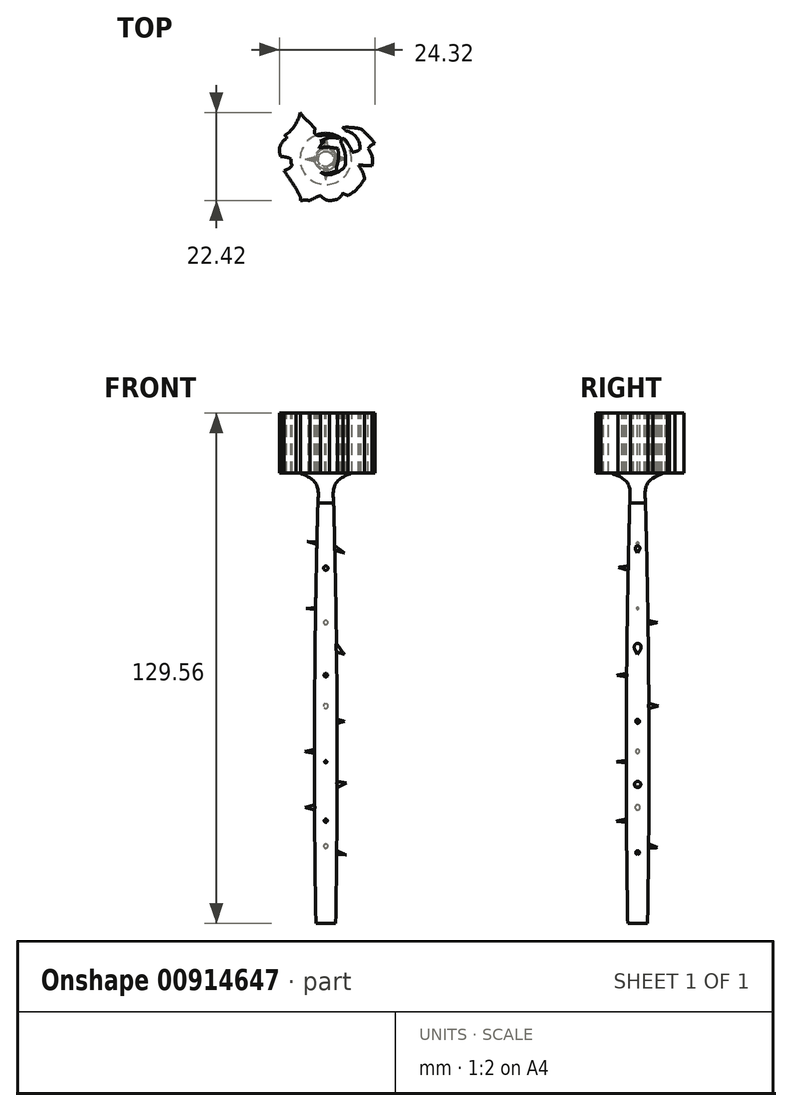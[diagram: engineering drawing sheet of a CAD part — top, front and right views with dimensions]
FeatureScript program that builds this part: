
annotation { "Feature Type Name" : "Feature", "Feature Type Description" : "" }
export const myFeature = defineFeature(function(context is Context, id is Id, definition is map)
    precondition{}
    {
        {
            var Q0;
            Q0=qCreatedBy(makeId("Front.planeOp"),FACE);
            var sketch = newSketch(context, id + "F0", { "sketchPlane" : qUnion([Q0])});
            skLineSegment(sketch, "E0", {"start": v(0, 50.56) * mm, "end": v(0, -56.14) * mm});
            skLineSegment(sketch, "E1", {"start": v(0, 50.56) * mm, "end": v(-2, 50.56) * mm});
            skLineSegment(sketch, "E2", {"start": v(0, -56.14) * mm, "end": v(-2.52, -56.14) * mm});
            skArc(sketch, "E3", {"start": v(-2, 50.56) * mm, "mid": v(-2.86, -2.8) * mm, "end": v(-2.52, -56.14) * mm});
            skLineSegment(sketch, "E4", {"start": v(0, 50.56) * mm, "end": v(0, -56.14) * mm, "construction": true});
            skSolve(sketch);
        }
        {
            var Q0;
            Q0=makeQuery(id+"F0.imprint","IMPRINT",FACE,{"disambiguationData":[TD([[makeQuery(id+"F0.imprint","IMPRINT",EDGE,{"derivedFrom":sQuery(id+"F0.wireOp",EDGE,"E0")}),-1.0]])]});
            var Q1;
            Q1=sQuery(id+"F0.wireOp",EDGE,"E0");
            revolve(context, id + "F1", {"surfaceOperationType" : NewSurfaceOperationType.NEW, "entities" : qUnion([Q0]), "axis" : qUnion([Q1]), "revolveType" : RevolveType.FULL});
        }
        {
            var Q0;
            Q0=qCreatedBy(makeId("Front.planeOp"),FACE);
            var sketch = newSketch(context, id + "F2", { "sketchPlane" : qUnion([Q0])});
            skLineSegment(sketch, "E5", {"start": v(-2.2, 40.38) * mm, "end": v(-2.19, 40.64) * mm});
            skLineSegment(sketch, "E6", {"start": v(-2.2, 40.38) * mm, "end": v(-4.73, 40.83) * mm});
            skLineSegment(sketch, "E7", {"start": v(2.21, 39.1) * mm, "end": v(4.78, 37.88) * mm});
            skLineSegment(sketch, "E8", {"start": v(4.78, 37.88) * mm, "end": v(2.24, 39.78) * mm});
            skLineSegment(sketch, "E9", {"start": v(-2.48, 24.12) * mm, "end": v(-5.02, 23.87) * mm});
            skLineSegment(sketch, "E10", {"start": v(-5.02, 23.87) * mm, "end": v(-2.48, 23.84) * mm});
            skLineSegment(sketch, "E11", {"start": v(-2.48, 23.84) * mm, "end": v(-2.48, 24.12) * mm});
            skLineSegment(sketch, "E12", {"start": v(2.24, 39.78) * mm, "end": v(2.21, 39.1) * mm});
            skLineSegment(sketch, "E13", {"start": v(-2.19, 40.64) * mm, "end": v(-4.73, 40.83) * mm});
            skLineSegment(sketch, "E14", {"start": v(2.24, 15.55) * mm, "end": v(2.24, 13.97) * mm});
            skLineSegment(sketch, "E15", {"start": v(2.24, 13.97) * mm, "end": v(4.78, 12.08) * mm});
            skLineSegment(sketch, "E16", {"start": v(4.78, 12.08) * mm, "end": v(2.24, 15.55) * mm});
            skLineSegment(sketch, "E17", {"start": v(2.24, -4.22) * mm, "end": v(4.78, -4.87) * mm});
            skLineSegment(sketch, "E18", {"start": v(4.78, -4.87) * mm, "end": v(2.75, -4.87) * mm});
            skLineSegment(sketch, "E19", {"start": v(-2.78, -11.98) * mm, "end": v(-5.32, -12.55) * mm});
            skLineSegment(sketch, "E20", {"start": v(-5.32, -12.55) * mm, "end": v(-2.8, -12.49) * mm});
            skLineSegment(sketch, "E21", {"start": v(-2.8, -12.49) * mm, "end": v(-2.78, -11.98) * mm});
            skLineSegment(sketch, "E22", {"start": v(2.7, -20.1) * mm, "end": v(5.25, -20.55) * mm});
            skLineSegment(sketch, "E23", {"start": v(5.25, -20.55) * mm, "end": v(2.8, -20.9) * mm});
            skLineSegment(sketch, "E24", {"start": v(2.8, -20.9) * mm, "end": v(2.7, -20.1) * mm});
            skLineSegment(sketch, "E25", {"start": v(-2.78, -26.09) * mm, "end": v(-5.32, -26.73) * mm});
            skLineSegment(sketch, "E26", {"start": v(-5.32, -26.73) * mm, "end": v(-2.78, -26.73) * mm});
            skLineSegment(sketch, "E27", {"start": v(-2.78, -26.73) * mm, "end": v(-2.78, -26.09) * mm});
            skLineSegment(sketch, "E28", {"start": v(2.7, -37.7) * mm, "end": v(5.25, -38.83) * mm});
            skLineSegment(sketch, "E29", {"start": v(5.25, -38.83) * mm, "end": v(2.7, -38.22) * mm});
            skLineSegment(sketch, "E30", {"start": v(2.7, -38.22) * mm, "end": v(2.7, -37.7) * mm});
            skLineSegment(sketch, "E31", {"start": v(-5.32, -26.73) * mm, "end": v(-2.78, -26.73) * mm, "construction": true});
            skLineSegment(sketch, "E32", {"start": v(5.25, -20.55) * mm, "end": v(2.8, -20.9) * mm, "construction": true});
            skLineSegment(sketch, "E33", {"start": v(5.25, -38.83) * mm, "end": v(2.7, -38.22) * mm, "construction": true});
            skLineSegment(sketch, "E34", {"start": v(-5.32, -12.55) * mm, "end": v(-2.8, -12.49) * mm, "construction": true});
            skLineSegment(sketch, "E35", {"start": v(4.78, -4.87) * mm, "end": v(2.75, -4.87) * mm, "construction": true});
            skLineSegment(sketch, "E36", {"start": v(2.24, 13.97) * mm, "end": v(4.78, 12.08) * mm, "construction": true});
            skLineSegment(sketch, "E37", {"start": v(-5.02, 23.87) * mm, "end": v(-2.48, 23.84) * mm, "construction": true});
            skLineSegment(sketch, "E38", {"start": v(4.78, 37.88) * mm, "end": v(2.24, 39.78) * mm, "construction": true});
            skLineSegment(sketch, "E39", {"start": v(-2.2, 40.38) * mm, "end": v(-4.73, 40.83) * mm, "construction": true});
            skLineSegment(sketch, "E40", {"start": v(2.75, -4.87) * mm, "end": v(2.24, -4.22) * mm});
            skSolve(sketch);
        }
        {
            var Q0;
            Q0=makeQuery(id+"F2.imprint","IMPRINT",FACE,{"disambiguationData":[TD([[makeQuery(id+"F2.imprint","IMPRINT",EDGE,{"derivedFrom":sQuery(id+"F2.wireOp",EDGE,"E28")}),-1.0]])]});
            var Q1;
            Q1=sQuery(id+"F2.wireOp",EDGE,"E29");
            revolve(context, id + "F3", {"operationType" : NewBodyOperationType.ADD, "surfaceOperationType" : NewSurfaceOperationType.NEW, "entities" : qUnion([Q0]), "axis" : qUnion([Q1]), "revolveType" : RevolveType.FULL});
        }
        {
            var Q0;
            Q0=makeQuery(id+"F2.imprint","IMPRINT",FACE,{"disambiguationData":[TD([[makeQuery(id+"F2.imprint","IMPRINT",EDGE,{"derivedFrom":sQuery(id+"F2.wireOp",EDGE,"E25")}),1.0]])]});
            var Q1;
            Q1=sQuery(id+"F2.wireOp",EDGE,"E26");
            revolve(context, id + "F4", {"operationType" : NewBodyOperationType.ADD, "surfaceOperationType" : NewSurfaceOperationType.NEW, "entities" : qUnion([Q0]), "axis" : qUnion([Q1]), "revolveType" : RevolveType.FULL});
        }
        {
            var Q0;
            Q0=makeQuery(id+"F2.imprint","IMPRINT",FACE,{"disambiguationData":[TD([[makeQuery(id+"F2.imprint","IMPRINT",EDGE,{"derivedFrom":sQuery(id+"F2.wireOp",EDGE,"E22")}),-1.0]])]});
            var Q1;
            Q1=sQuery(id+"F2.wireOp",EDGE,"E23");
            revolve(context, id + "F5", {"operationType" : NewBodyOperationType.ADD, "surfaceOperationType" : NewSurfaceOperationType.NEW, "entities" : qUnion([Q0]), "axis" : qUnion([Q1]), "revolveType" : RevolveType.FULL});
        }
        {
            var Q0;
            Q0=makeQuery(id+"F2.imprint","IMPRINT",FACE,{"disambiguationData":[TD([[makeQuery(id+"F2.imprint","IMPRINT",EDGE,{"derivedFrom":sQuery(id+"F2.wireOp",EDGE,"E19")}),1.0]])]});
            var Q1;
            Q1=sQuery(id+"F2.wireOp",EDGE,"E20");
            revolve(context, id + "F6", {"operationType" : NewBodyOperationType.ADD, "surfaceOperationType" : NewSurfaceOperationType.NEW, "entities" : qUnion([Q0]), "axis" : qUnion([Q1]), "revolveType" : RevolveType.FULL});
        }
        {
            var Q0;
            Q0=makeQuery(id+"F2.imprint","IMPRINT",FACE,{"disambiguationData":[TD([[makeQuery(id+"F2.imprint","IMPRINT",EDGE,{"derivedFrom":sQuery(id+"F2.wireOp",EDGE,"E17")}),-1.0]])]});
            var Q1;
            Q1=sQuery(id+"F2.wireOp",EDGE,"E18");
            revolve(context, id + "F7", {"operationType" : NewBodyOperationType.ADD, "surfaceOperationType" : NewSurfaceOperationType.NEW, "entities" : qUnion([Q0]), "axis" : qUnion([Q1]), "revolveType" : RevolveType.FULL});
        }
        {
            var Q0;
            Q0=makeQuery(id+"F2.imprint","IMPRINT",FACE,{"disambiguationData":[TD([[makeQuery(id+"F2.imprint","IMPRINT",EDGE,{"derivedFrom":sQuery(id+"F2.wireOp",EDGE,"E14")}),1.0]])]});
            var Q1;
            Q1=sQuery(id+"F2.wireOp",EDGE,"E15");
            revolve(context, id + "F8", {"operationType" : NewBodyOperationType.ADD, "surfaceOperationType" : NewSurfaceOperationType.NEW, "entities" : qUnion([Q0]), "axis" : qUnion([Q1]), "revolveType" : RevolveType.FULL});
        }
        {
            var Q0;
            Q0=makeQuery(id+"F2.imprint","IMPRINT",FACE,{"disambiguationData":[TD([[makeQuery(id+"F2.imprint","IMPRINT",EDGE,{"derivedFrom":sQuery(id+"F2.wireOp",EDGE,"E9")}),1.0]])]});
            var Q1;
            Q1=sQuery(id+"F2.wireOp",EDGE,"E10");
            revolve(context, id + "F9", {"operationType" : NewBodyOperationType.ADD, "surfaceOperationType" : NewSurfaceOperationType.NEW, "entities" : qUnion([Q0]), "axis" : qUnion([Q1]), "revolveType" : RevolveType.FULL});
        }
        {
            var Q0;
            Q0=makeQuery(id+"F2.imprint","IMPRINT",FACE,{"disambiguationData":[TD([[makeQuery(id+"F2.imprint","IMPRINT",EDGE,{"derivedFrom":sQuery(id+"F2.wireOp",EDGE,"E7")}),1.0]])]});
            var Q1;
            Q1=sQuery(id+"F2.wireOp",EDGE,"E7");
            revolve(context, id + "F10", {"operationType" : NewBodyOperationType.ADD, "surfaceOperationType" : NewSurfaceOperationType.NEW, "entities" : qUnion([Q0]), "axis" : qUnion([Q1]), "revolveType" : RevolveType.FULL});
        }
        {
            var Q0;
            Q0=makeQuery(id+"F2.imprint","IMPRINT",FACE,{"disambiguationData":[TD([[makeQuery(id+"F2.imprint","IMPRINT",EDGE,{"derivedFrom":sQuery(id+"F2.wireOp",EDGE,"E5")}),1.0]])]});
            var Q1;
            Q1=sQuery(id+"F2.wireOp",EDGE,"E6");
            revolve(context, id + "F11", {"operationType" : NewBodyOperationType.ADD, "surfaceOperationType" : NewSurfaceOperationType.NEW, "entities" : qUnion([Q0]), "axis" : qUnion([Q1]), "revolveType" : RevolveType.FULL});
        }
        {
            var Q0;
            Q0=qCreatedBy(makeId("Right.planeOp"),FACE);
            var sketch = newSketch(context, id + "F12", { "sketchPlane" : qUnion([Q0])});
            skLineSegment(sketch, "E41", {"start": v(-2.3, 34.62) * mm, "end": v(-4.83, 34.27) * mm});
            skLineSegment(sketch, "E42", {"start": v(-4.83, 34.27) * mm, "end": v(-2.3, 34.06) * mm});
            skLineSegment(sketch, "E43", {"start": v(-2.3, 34.06) * mm, "end": v(-2.3, 34.62) * mm});
            skLineSegment(sketch, "E44", {"start": v(2.44, 20.8) * mm, "end": v(4.98, 20.23) * mm});
            skLineSegment(sketch, "E45", {"start": v(4.98, 20.23) * mm, "end": v(2.51, 20.23) * mm});
            skLineSegment(sketch, "E46", {"start": v(2.51, 20.23) * mm, "end": v(2.44, 20.8) * mm});
            skLineSegment(sketch, "E47", {"start": v(-2.7, 7.32) * mm, "end": v(-5.25, 6.85) * mm});
            skLineSegment(sketch, "E48", {"start": v(-5.25, 6.85) * mm, "end": v(-2.7, 6.85) * mm});
            skLineSegment(sketch, "E49", {"start": v(-2.7, 6.85) * mm, "end": v(-2.7, 7.32) * mm});
            skLineSegment(sketch, "E50", {"start": v(-2.82, -14.85) * mm, "end": v(-5.36, -15.13) * mm});
            skLineSegment(sketch, "E51", {"start": v(-5.36, -15.13) * mm, "end": v(-2.83, -15.13) * mm});
            skLineSegment(sketch, "E52", {"start": v(-2.83, -15.13) * mm, "end": v(-2.82, -14.85) * mm});
            skLineSegment(sketch, "E53", {"start": v(-2.86, -29.71) * mm, "end": v(-5.4, -30.23) * mm});
            skLineSegment(sketch, "E54", {"start": v(-5.4, -30.23) * mm, "end": v(-2.8, -30.1) * mm});
            skLineSegment(sketch, "E55", {"start": v(-2.8, -30.1) * mm, "end": v(-2.86, -29.71) * mm});
            skLineSegment(sketch, "E56", {"start": v(2.65, -0.32) * mm, "end": v(5.25, -0.97) * mm});
            skLineSegment(sketch, "E57", {"start": v(5.25, -0.97) * mm, "end": v(2.71, -0.97) * mm});
            skLineSegment(sketch, "E58", {"start": v(2.71, -0.97) * mm, "end": v(2.65, -0.32) * mm});
            skLineSegment(sketch, "E59", {"start": v(2.54, -35.96) * mm, "end": v(5.08, -36.94) * mm});
            skLineSegment(sketch, "E60", {"start": v(5.08, -36.94) * mm, "end": v(2.6, -36.57) * mm});
            skLineSegment(sketch, "E61", {"start": v(2.6, -36.57) * mm, "end": v(2.54, -35.96) * mm});
            skSolve(sketch);
        }
        {
            var Q0;
            Q0=makeQuery(id+"F12.imprint","IMPRINT",FACE,{"disambiguationData":[TD([[makeQuery(id+"F12.imprint","IMPRINT",EDGE,{"derivedFrom":sQuery(id+"F12.wireOp",EDGE,"E59")}),-1.0]])]});
            var Q1;
            Q1=sQuery(id+"F12.wireOp",EDGE,"E60");
            revolve(context, id + "F13", {"operationType" : NewBodyOperationType.ADD, "surfaceOperationType" : NewSurfaceOperationType.NEW, "entities" : qUnion([Q0]), "axis" : qUnion([Q1]), "revolveType" : RevolveType.FULL});
        }
        {
            var Q0;
            Q0=makeQuery(id+"F12.imprint","IMPRINT",FACE,{"disambiguationData":[TD([[makeQuery(id+"F12.imprint","IMPRINT",EDGE,{"derivedFrom":sQuery(id+"F12.wireOp",EDGE,"E53")}),1.0]])]});
            var Q1;
            Q1=sQuery(id+"F12.wireOp",EDGE,"E54");
            revolve(context, id + "F14", {"operationType" : NewBodyOperationType.ADD, "surfaceOperationType" : NewSurfaceOperationType.NEW, "entities" : qUnion([Q0]), "axis" : qUnion([Q1]), "revolveType" : RevolveType.FULL});
        }
        {
            var Q0;
            Q0=makeQuery(id+"F12.imprint","IMPRINT",FACE,{"disambiguationData":[TD([[makeQuery(id+"F12.imprint","IMPRINT",EDGE,{"derivedFrom":sQuery(id+"F12.wireOp",EDGE,"E50")}),1.0]])]});
            var Q1;
            Q1=sQuery(id+"F12.wireOp",EDGE,"E51");
            revolve(context, id + "F15", {"operationType" : NewBodyOperationType.ADD, "surfaceOperationType" : NewSurfaceOperationType.NEW, "entities" : qUnion([Q0]), "axis" : qUnion([Q1]), "revolveType" : RevolveType.FULL});
        }
        {
            var Q0;
            Q0=makeQuery(id+"F12.imprint","IMPRINT",FACE,{"disambiguationData":[TD([[makeQuery(id+"F12.imprint","IMPRINT",EDGE,{"derivedFrom":sQuery(id+"F12.wireOp",EDGE,"E56")}),-1.0]])]});
            var Q1;
            Q1=sQuery(id+"F12.wireOp",EDGE,"E57");
            revolve(context, id + "F16", {"operationType" : NewBodyOperationType.ADD, "surfaceOperationType" : NewSurfaceOperationType.NEW, "entities" : qUnion([Q0]), "axis" : qUnion([Q1]), "revolveType" : RevolveType.FULL});
        }
        {
            var Q0;
            Q0=makeQuery(id+"F12.imprint","IMPRINT",FACE,{"disambiguationData":[TD([[makeQuery(id+"F12.imprint","IMPRINT",EDGE,{"derivedFrom":sQuery(id+"F12.wireOp",EDGE,"E47")}),1.0]])]});
            var Q1;
            Q1=sQuery(id+"F12.wireOp",EDGE,"E48");
            revolve(context, id + "F17", {"operationType" : NewBodyOperationType.ADD, "surfaceOperationType" : NewSurfaceOperationType.NEW, "entities" : qUnion([Q0]), "axis" : qUnion([Q1]), "revolveType" : RevolveType.FULL});
        }
        {
            var Q0;
            Q0=makeQuery(id+"F12.imprint","IMPRINT",FACE,{"disambiguationData":[TD([[makeQuery(id+"F12.imprint","IMPRINT",EDGE,{"derivedFrom":sQuery(id+"F12.wireOp",EDGE,"E44")}),-1.0]])]});
            var Q1;
            Q1=sQuery(id+"F12.wireOp",EDGE,"E45");
            revolve(context, id + "F18", {"operationType" : NewBodyOperationType.ADD, "surfaceOperationType" : NewSurfaceOperationType.NEW, "entities" : qUnion([Q0]), "axis" : qUnion([Q1]), "revolveType" : RevolveType.FULL});
        }
        {
            var Q0;
            Q0=makeQuery(id+"F12.imprint","IMPRINT",FACE,{"disambiguationData":[TD([[makeQuery(id+"F12.imprint","IMPRINT",EDGE,{"derivedFrom":sQuery(id+"F12.wireOp",EDGE,"E41")}),1.0]])]});
            var Q1;
            Q1=sQuery(id+"F12.wireOp",EDGE,"E42");
            revolve(context, id + "F19", {"operationType" : NewBodyOperationType.ADD, "surfaceOperationType" : NewSurfaceOperationType.NEW, "entities" : qUnion([Q0]), "axis" : qUnion([Q1]), "revolveType" : RevolveType.FULL});
        }
        {
            var Q0;
            Q0=makeQuery(id+"F1.opRevolve","SWEPT_FACE",FACE,{"disambiguationData":[OSD([sQuery(id+"F0.wireOp",EDGE,"E1")])]});
            cPlane(context, id + "F20", {"entities" : qUnion([Q0]), "cplaneType" : CPlaneType.OFFSET, "offset" : 76.2 * mm, "width" : 152.4 * mm, "height" : 152.4 * mm});
        }
        {
            var Q0;
            Q0=makeQuery(id+"F1.opRevolve","SWEPT_FACE",FACE,{"disambiguationData":[OSD([sQuery(id+"F0.wireOp",EDGE,"E1")])]});
            cPlane(context, id + "F21", {"entities" : qUnion([Q0]), "cplaneType" : CPlaneType.OFFSET, "offset" : 22.86 * mm, "width" : 152.4 * mm, "height" : 152.4 * mm});
        }
        {
            var Q0;
            Q0=qCreatedBy(id+"F21.planeOp",FACE);
            var sketch = newSketch(context, id + "F22", { "sketchPlane" : qUnion([Q0])});
            skCircle(sketch, "E62", {"center": v(0, 0) * mm, "radius": 10.65 * mm});
            skLineSegment(sketch, "E63", {"start": v(0, 10.65) * mm, "end": v(0, -10.65) * mm, "construction": true});
            skSolve(sketch);
        }
        {
            var Q0;
            Q0=makeQuery(id+"F22.imprint","IMPRINT",FACE,{"disambiguationData":[TD([[makeQuery(id+"F22.imprint","IMPRINT",EDGE,{"derivedFrom":sQuery(id+"F22.wireOp",EDGE,"E62")}),1.0]])]});
            cPlane(context, id + "F23", {"entities" : qUnion([Q0]), "cplaneType" : CPlaneType.OFFSET, "offset" : 15.24 * mm, "oppositeDirection" : true, "width" : 152.4 * mm, "height" : 152.4 * mm});
        }
        {
            var Q0;
            Q0=qCreatedBy(id+"F23.planeOp",FACE);
            var sketch = newSketch(context, id + "F24", { "sketchPlane" : qUnion([Q0])});
            skCircle(sketch, "E64", {"center": v(0, 0) * mm, "radius": 6.51 * mm});
            skSolve(sketch);
        }
        {
            var Q0;
            Q0=makeQuery(id+"F22.imprint","IMPRINT",FACE,{"disambiguationData":[TD([[makeQuery(id+"F22.imprint","IMPRINT",EDGE,{"derivedFrom":sQuery(id+"F22.wireOp",EDGE,"E62")}),1.0]])]});
            cPlane(context, id + "F25", {"entities" : qUnion([Q0]), "cplaneType" : CPlaneType.OFFSET, "offset" : 17.78 * mm, "oppositeDirection" : true, "width" : 152.4 * mm, "height" : 152.4 * mm});
        }
        {
            var Q0;
            Q0=qCreatedBy(id+"F25.planeOp",FACE);
            var sketch = newSketch(context, id + "F26", { "sketchPlane" : qUnion([Q0])});
            skCircle(sketch, "E65", {"center": v(0, 0) * mm, "radius": 2.54 * mm});
            skSolve(sketch);
        }
        {
            var Q1;
            Q1=makeQuery(id+"F1.opRevolve","SWEPT_FACE",FACE,{"disambiguationData":[OSD([sQuery(id+"F0.wireOp",EDGE,"E1")])]});
            var Q2;
            Q2=makeQuery(id+"F26.imprint","IMPRINT",FACE,{"disambiguationData":[TD([[makeQuery(id+"F26.imprint","IMPRINT",EDGE,{"derivedFrom":sQuery(id+"F26.wireOp",EDGE,"E65")}),1.0]])]});
            var Q3;
            Q3=makeQuery(id+"F24.imprint","IMPRINT",FACE,{"disambiguationData":[TD([[makeQuery(id+"F24.imprint","IMPRINT",EDGE,{"derivedFrom":sQuery(id+"F24.wireOp",EDGE,"E64")}),1.0]])]});
            loft(context, id + "F27", {"operationType" : NewBodyOperationType.ADD, "sheetProfilesArray" : [{ "sheetProfileEntities" : qUnion([Q1]) }, { "sheetProfileEntities" : qUnion([Q2]) }, { "sheetProfileEntities" : qUnion([Q3]) }]});
        }
        {
            var Q0;
            Q0=sQuery(id+"F22.wireOp",EDGE,"E63");
            cPlane(context, id + "F28", {"entities" : qUnion([Q0]), "cplaneType" : CPlaneType.LINE_ANGLE, "offset" : 25.4 * mm, "angle" : 90 * degree, "width" : 152.4 * mm, "height" : 152.4 * mm});
        }
        {
            var Q0;
            Q0=makeQuery(id+"F22.imprint","IMPRINT",FACE,{"disambiguationData":[TD([[makeQuery(id+"F22.imprint","IMPRINT",EDGE,{"derivedFrom":sQuery(id+"F22.wireOp",EDGE,"E62")}),1.0]])]});
            var sketch = newSketch(context, id + "F29", { "sketchPlane" : qUnion([Q0])});
            skArc(sketch, "E66", {"start": v(-10.3, 6.03) * mm, "mid": v(-7.83, 8.55) * mm, "end": v(-6.5, 11.82) * mm});
            skArc(sketch, "E67", {"start": v(-10.3, 6.03) * mm, "mid": v(-10.2, 5.76) * mm, "end": v(-9.93, 5.67) * mm});
            skArc(sketch, "E68", {"start": v(-10.05, 5.2) * mm, "mid": v(-9.93, 5.42) * mm, "end": v(-9.93, 5.67) * mm});
            skArc(sketch, "E69", {"start": v(-10.05, 5.2) * mm, "mid": v(-11.26, 3.94) * mm, "end": v(-11.8, 2.28) * mm});
            skArc(sketch, "E70", {"start": v(-11.8, 2.28) * mm, "mid": v(-11.68, 1.4) * mm, "end": v(-11.44, 0.54) * mm});
            skArc(sketch, "E71", {"start": v(-8.89, 0) * mm, "mid": v(-10.12, 0.48) * mm, "end": v(-11.44, 0.54) * mm});
            skLineSegment(sketch, "E72", {"start": v(-8.89, 0) * mm, "end": v(-8.89, -1.06) * mm});
            skArc(sketch, "E73", {"start": v(-8.56, -1.63) * mm, "mid": v(-8.7, -1.33) * mm, "end": v(-8.89, -1.06) * mm});
            skArc(sketch, "E74", {"start": v(-10.65, -2.93) * mm, "mid": v(-9.48, -2.49) * mm, "end": v(-8.56, -1.63) * mm});
            skArc(sketch, "E75", {"start": v(-7.62, -7.46) * mm, "mid": v(-9.12, -5.18) * mm, "end": v(-10.65, -2.93) * mm});
            skArc(sketch, "E76", {"start": v(-6.36, -9.89) * mm, "mid": v(-6.95, -8.66) * mm, "end": v(-7.62, -7.46) * mm});
            skLineSegment(sketch, "E77", {"start": v(-6.36, -9.89) * mm, "end": v(-6.36, -10.57) * mm});
            skArc(sketch, "E78", {"start": v(-4, -10.57) * mm, "mid": v(-5.17, -10.48) * mm, "end": v(-6.36, -10.57) * mm});
            skArc(sketch, "E79", {"start": v(-1.28, -9.28) * mm, "mid": v(-2.67, -9.85) * mm, "end": v(-4, -10.57) * mm});
            skArc(sketch, "E80", {"start": v(-1.28, -9.28) * mm, "mid": v(1.7, -10.61) * mm, "end": v(4.36, -8.71) * mm});
            skArc(sketch, "E81", {"start": v(4.36, -8.71) * mm, "mid": v(4.99, -9.03) * mm, "end": v(5.65, -9.28) * mm});
            skArc(sketch, "E82", {"start": v(5.65, -9.28) * mm, "mid": v(8.09, -7.47) * mm, "end": v(9.83, -4.97) * mm});
            skArc(sketch, "E83", {"start": v(9.83, -4.97) * mm, "mid": v(8.82, -2.33) * mm, "end": v(6.88, -0.27) * mm});
            skArc(sketch, "E84", {"start": v(11.73, -1.76) * mm, "mid": v(11.8, 0.54) * mm, "end": v(10.78, 2.6) * mm});
            skArc(sketch, "E85", {"start": v(12.51, 3.95) * mm, "mid": v(11.51, 3.45) * mm, "end": v(10.78, 2.6) * mm});
            skArc(sketch, "E86", {"start": v(12.51, 3.95) * mm, "mid": v(10.8, 5.87) * mm, "end": v(8.9, 7.6) * mm});
            skArc(sketch, "E87", {"start": v(5.56, -2.84) * mm, "mid": v(6.42, -1.66) * mm, "end": v(6.88, -0.27) * mm});
            skArc(sketch, "E88", {"start": v(3.92, -6.76) * mm, "mid": v(5.27, -5.02) * mm, "end": v(5.56, -2.84) * mm});
            skArc(sketch, "E89", {"start": v(2.15, -7.14) * mm, "mid": v(3.07, -7.08) * mm, "end": v(3.92, -6.76) * mm});
            skArc(sketch, "E90", {"start": v(1.36, -5.2) * mm, "mid": v(1.56, -6.25) * mm, "end": v(2.15, -7.14) * mm});
            skArc(sketch, "E91", {"start": v(1.36, -5.2) * mm, "mid": v(3.35, -3.67) * mm, "end": v(4.93, -1.71) * mm});
            skArc(sketch, "E92", {"start": v(-8.56, -1.63) * mm, "mid": v(-7.28, -5.09) * mm, "end": v(-4.83, -7.84) * mm});
            skArc(sketch, "E93", {"start": v(-7.2, 4.12) * mm, "mid": v(-8.45, 2.22) * mm, "end": v(-8.89, 0) * mm});
            skArc(sketch, "E94", {"start": v(-4.73, 3.74) * mm, "mid": v(-5.9, 4.4) * mm, "end": v(-7.2, 4.12) * mm});
            skArc(sketch, "E95", {"start": v(-4.73, 3.74) * mm, "mid": v(-6, 2.09) * mm, "end": v(-6.08, 0) * mm});
            skArc(sketch, "E96", {"start": v(-4.83, -7.84) * mm, "mid": v(-3.56, -8.21) * mm, "end": v(-2.4, -7.56) * mm});
            skArc(sketch, "E97", {"start": v(-2.4, -7.56) * mm, "mid": v(-1.92, -8.48) * mm, "end": v(-1.28, -9.28) * mm});
            skArc(sketch, "E98", {"start": v(6.88, -0.27) * mm, "mid": v(6.72, 1.76) * mm, "end": v(5.8, 3.57) * mm});
            skArc(sketch, "E99", {"start": v(5.8, 3.57) * mm, "mid": v(5.3, 4.44) * mm, "end": v(4.63, 5.18) * mm});
            skArc(sketch, "E100", {"start": v(1.25, 6.13) * mm, "mid": v(-2.02, 5.64) * mm, "end": v(-4.73, 3.74) * mm});
            skArc(sketch, "E101", {"start": v(3.36, 5.68) * mm, "mid": v(2.32, 5.95) * mm, "end": v(1.25, 6.13) * mm});
            skArc(sketch, "E102", {"start": v(-2.4, -7.56) * mm, "mid": v(-1.73, -5.47) * mm, "end": v(-1.99, -3.3) * mm});
            skArc(sketch, "E103", {"start": v(-4.6, -2.9) * mm, "mid": v(-3.3, -3.16) * mm, "end": v(-1.99, -3.3) * mm});
            skArc(sketch, "E104", {"start": v(-6.2, -1.06) * mm, "mid": v(-5.5, -2.09) * mm, "end": v(-4.57, -2.9) * mm});
            skArc(sketch, "E105", {"start": v(-5.73, -0.44) * mm, "mid": v(-6.11, -0.64) * mm, "end": v(-6.2, -1.06) * mm});
            skArc(sketch, "E106", {"start": v(-4.81, -0.44) * mm, "mid": v(-5.27, -0.37) * mm, "end": v(-5.73, -0.44) * mm});
            skArc(sketch, "E107", {"start": v(0, -4.03) * mm, "mid": v(2.76, -3.5) * mm, "end": v(4.93, -1.71) * mm});
            skArc(sketch, "E108", {"start": v(-1.28, -3.35) * mm, "mid": v(-0.68, -3.77) * mm, "end": v(0, -4.03) * mm});
            skLineSegment(sketch, "E109", {"start": v(-1.28, -3.35) * mm, "end": v(-1.99, -3.3) * mm});
            skArc(sketch, "E110", {"start": v(4.93, -1.71) * mm, "mid": v(4.7, -1.45) * mm, "end": v(4.37, -1.51) * mm});
            skArc(sketch, "E111", {"start": v(1, -3.54) * mm, "mid": v(2.87, -2.83) * mm, "end": v(4.37, -1.51) * mm});
            skArc(sketch, "E112", {"start": v(-2.3, -0.52) * mm, "mid": v(-0.84, -2.24) * mm, "end": v(1, -3.54) * mm});
            skArc(sketch, "E113", {"start": v(-2.48, 0.28) * mm, "mid": v(-2.5, -0.15) * mm, "end": v(-2.3, -0.52) * mm});
            skArc(sketch, "E114", {"start": v(-0.24, 4.56) * mm, "mid": v(-1.82, 2.66) * mm, "end": v(-2.48, 0.28) * mm});
            skArc(sketch, "E115", {"start": v(-6.08, 0) * mm, "mid": v(-5.6, -0.11) * mm, "end": v(-5.14, 0.05) * mm});
            skArc(sketch, "E116", {"start": v(-1.98, 4.15) * mm, "mid": v(-3.9, 2.37) * mm, "end": v(-5.14, 0.05) * mm});
            skLineSegment(sketch, "E117", {"start": v(-1.98, 4.15) * mm, "end": v(-1.4, 4.53) * mm});
            skArc(sketch, "E118", {"start": v(-0.24, 4.56) * mm, "mid": v(-0.83, 4.7) * mm, "end": v(-1.4, 4.53) * mm});
            skArc(sketch, "E119", {"start": v(-1.28, -3.35) * mm, "mid": v(-3, -1.83) * mm, "end": v(-4.81, -0.44) * mm});
            skArc(sketch, "E120", {"start": v(-1.28, -3.35) * mm, "mid": v(-0.16, -3.68) * mm, "end": v(1, -3.54) * mm});
            skArc(sketch, "E121", {"start": v(3.05, 2.64) * mm, "mid": v(0.67, 2.96) * mm, "end": v(-1.74, 2.82) * mm});
            skArc(sketch, "E122", {"start": v(3.19, 1.77) * mm, "mid": v(3.14, 2.2) * mm, "end": v(3.05, 2.64) * mm});
            skArc(sketch, "E123", {"start": v(2.75, -1.95) * mm, "mid": v(3.2, -0.12) * mm, "end": v(3.19, 1.77) * mm});
            skArc(sketch, "E124", {"start": v(2.75, -1.95) * mm, "mid": v(2.68, -2.42) * mm, "end": v(2.75, -2.9) * mm});
            skArc(sketch, "E125", {"start": v(4.63, 5.18) * mm, "mid": v(3.96, 4.83) * mm, "end": v(3.9, 4.08) * mm});
            skArc(sketch, "E126", {"start": v(4.93, -1.71) * mm, "mid": v(4.93, 1.28) * mm, "end": v(3.9, 4.08) * mm});
            skArc(sketch, "E127", {"start": v(3.36, 5.18) * mm, "mid": v(0.9, 5.4) * mm, "end": v(-1.4, 4.53) * mm});
            skArc(sketch, "E128", {"start": v(3.36, 5.18) * mm, "mid": v(3.42, 5.43) * mm, "end": v(3.36, 5.68) * mm});
            skArc(sketch, "E129", {"start": v(2.47, -0.15) * mm, "mid": v(2.7, 1.37) * mm, "end": v(2.2, 2.81) * mm});
            skArc(sketch, "E130", {"start": v(-0.62, 0) * mm, "mid": v(0.91, -0.4) * mm, "end": v(2.47, -0.15) * mm});
            skArc(sketch, "E131", {"start": v(-0.4, 1.64) * mm, "mid": v(-0.58, 0.83) * mm, "end": v(-0.62, 0) * mm});
            skArc(sketch, "E132", {"start": v(0.65, 1.9) * mm, "mid": v(0.08, 1.95) * mm, "end": v(-0.4, 1.64) * mm});
            skArc(sketch, "E133", {"start": v(1.37, 1.25) * mm, "mid": v(1.07, 1.65) * mm, "end": v(0.65, 1.9) * mm});
            skArc(sketch, "E134", {"start": v(1.2, 0.69) * mm, "mid": v(1.35, 0.95) * mm, "end": v(1.37, 1.25) * mm});
            skArc(sketch, "E135", {"start": v(0.48, 0.5) * mm, "mid": v(0.86, 0.53) * mm, "end": v(1.2, 0.69) * mm});
            skArc(sketch, "E136", {"start": v(-0.06, 0.87) * mm, "mid": v(0.18, 0.63) * mm, "end": v(0.48, 0.5) * mm});
            skArc(sketch, "E137", {"start": v(0.33, 1.25) * mm, "mid": v(0.08, 1.11) * mm, "end": v(-0.06, 0.87) * mm});
            skArc(sketch, "E138", {"start": v(0.84, 1.17) * mm, "mid": v(0.6, 1.26) * mm, "end": v(0.33, 1.25) * mm});
            skArc(sketch, "E139", {"start": v(0.65, 0.98) * mm, "mid": v(0.8, 1.02) * mm, "end": v(0.85, 1.17) * mm});
            skLineSegment(sketch, "E140", {"start": v(-4.38, 9.46) * mm, "end": v(-2.59, 7.63) * mm});
            skArc(sketch, "E141", {"start": v(-2.59, 7.63) * mm, "mid": v(-2.88, 6.66) * mm, "end": v(-2.12, 5.99) * mm});
            skArc(sketch, "E142", {"start": v(-2.12, 5.99) * mm, "mid": v(-1.68, 5.91) * mm, "end": v(-1.24, 5.9) * mm});
            skArc(sketch, "E143", {"start": v(-1.02, 7.72) * mm, "mid": v(-1.82, 8.02) * mm, "end": v(-2.59, 7.63) * mm});
            skArc(sketch, "E144", {"start": v(0.74, 8.83) * mm, "mid": v(-0.28, 8.5) * mm, "end": v(-1.02, 7.72) * mm});
            skArc(sketch, "E145", {"start": v(3.72, 8.2) * mm, "mid": v(2.3, 8.82) * mm, "end": v(0.74, 8.83) * mm});
            skArc(sketch, "E146", {"start": v(5.1, 7.12) * mm, "mid": v(4.52, 7.8) * mm, "end": v(3.72, 8.2) * mm});
            skArc(sketch, "E147", {"start": v(8.7, 2.44) * mm, "mid": v(7.79, 5.46) * mm, "end": v(5.1, 7.12) * mm});
            skArc(sketch, "E148", {"start": v(6.72, 1.76) * mm, "mid": v(7.77, 1.94) * mm, "end": v(8.7, 2.44) * mm});
            skArc(sketch, "E149", {"start": v(-6.5, 11.82) * mm, "mid": v(-5.58, 10.52) * mm, "end": v(-4.38, 9.46) * mm});
            skArc(sketch, "E150", {"start": v(3.92, -6.76) * mm, "mid": v(3.88, -7.8) * mm, "end": v(4.36, -8.71) * mm});
            skArc(sketch, "E151", {"start": v(11.73, -1.76) * mm, "mid": v(10.02, -1.64) * mm, "end": v(8.3, -1.62) * mm});
            skArc(sketch, "E152", {"start": v(8.9, 7.6) * mm, "mid": v(6.59, 7.98) * mm, "end": v(4.23, 7.99) * mm});
            skSolve(sketch);
        }
        {
            var Q0;
            {var subQ1=sQuery(id+"F29.wireOp",EDGE,"E84");Q0=makeQuery(id+"F29.imprint","IMPRINT",FACE,{"disambiguationData":[TD([[makeQuery(id+"F29.imprint","IMPRINT",EDGE,{"derivedFrom":subQ1}),1.0]])]});}
            var Q1;
            {var subQ0=sQuery(id+"F29.wireOp",EDGE,"E76");Q1=makeQuery(id+"F29.imprint","IMPRINT",FACE,{"disambiguationData":[TD([[makeQuery(id+"F29.imprint","IMPRINT",EDGE,{"derivedFrom":subQ0}),-1.0]])]});}
            var Q2;
            {var subQ0=sQuery(id+"F29.wireOp",EDGE,"E75");var subQ1=sQuery(id+"F29.wireOp",EDGE,"E74");var subQ2=makeQuery(id+"F29.imprint","INTERSECT",VERTEX,{"derivedFrom":[subQ1,subQ0]});Q2=makeQuery(id+"F29.imprint","IMPRINT",FACE,{"disambiguationData":[TD([[makeQuery(id+"F29.imprint","IMPRINT",EDGE,{"disambiguationData":[TD([[subQ2,-1.0]])],"derivedFrom":subQ1}),-1.0]])]});}
            var Q3;
            {var subQ0=sQuery(id+"F29.wireOp",EDGE,"E82");Q3=makeQuery(id+"F29.imprint","IMPRINT",FACE,{"disambiguationData":[TD([[makeQuery(id+"F29.imprint","IMPRINT",EDGE,{"derivedFrom":subQ0}),1.0]])]});}
            var Q4;
            {var subQ0=sQuery(id+"F29.wireOp",EDGE,"E66");Q4=makeQuery(id+"F29.imprint","IMPRINT",FACE,{"disambiguationData":[TD([[makeQuery(id+"F29.imprint","IMPRINT",EDGE,{"derivedFrom":subQ0}),-1.0]])]});}
            extrude(context, id + "F30", {"entities" : qUnion([Q0, Q1, Q2, Q3, Q4]), "operationType" : NewBodyOperationType.ADD, "oppositeDirection" : true, "depth" : 15.24 * mm, "offsetDistance" : 25.4 * mm});
        }
        {
            var Q0;
            {var subQ3=sQuery(id+"F29.wireOp",EDGE,"E93");Q0=makeQuery(id+"F29.imprint","IMPRINT",FACE,{"disambiguationData":[TD([[makeQuery(id+"F29.imprint","IMPRINT",EDGE,{"derivedFrom":subQ3}),-1.0]])]});}
            var Q1;
            {var subQ2=sQuery(id+"F29.wireOp",EDGE,"E95");Q1=makeQuery(id+"F29.imprint","IMPRINT",FACE,{"disambiguationData":[TD([[makeQuery(id+"F29.imprint","IMPRINT",EDGE,{"derivedFrom":subQ2}),1.0]])]});}
            var Q2;
            Q2=makeQuery(id+"F29.imprint","IMPRINT",FACE,{"disambiguationData":[TD([[makeQuery(id+"F29.imprint","IMPRINT",EDGE,{"derivedFrom":sQuery(id+"F29.wireOp",EDGE,"E72")}),1.0]])]});
            var Q3;
            {var subQ0=sQuery(id+"F29.wireOp",EDGE,"E92");Q3=makeQuery(id+"F29.imprint","IMPRINT",FACE,{"disambiguationData":[TD([[makeQuery(id+"F29.imprint","IMPRINT",EDGE,{"derivedFrom":subQ0}),-1.0]])]});}
            var Q4;
            {var subQ0=sQuery(id+"F29.wireOp",EDGE,"E87");Q4=makeQuery(id+"F29.imprint","IMPRINT",FACE,{"disambiguationData":[TD([[makeQuery(id+"F29.imprint","IMPRINT",EDGE,{"derivedFrom":subQ0}),-1.0]])]});}
            var Q5;
            {var subQ0=sQuery(id+"F29.wireOp",EDGE,"E82");Q5=makeQuery(id+"F29.imprint","IMPRINT",FACE,{"disambiguationData":[TD([[makeQuery(id+"F29.imprint","IMPRINT",EDGE,{"derivedFrom":subQ0}),1.0]])]});}
            var Q6;
            {var subQ1=sQuery(id+"F29.wireOp",EDGE,"E112");Q6=makeQuery(id+"F29.imprint","IMPRINT",FACE,{"disambiguationData":[TD([[makeQuery(id+"F29.imprint","IMPRINT",EDGE,{"derivedFrom":subQ1}),1.0]])]});}
            var Q7;
            {var subQ3=sQuery(id+"F29.wireOp",EDGE,"E87");Q7=makeQuery(id+"F29.imprint","IMPRINT",FACE,{"disambiguationData":[TD([[makeQuery(id+"F29.imprint","IMPRINT",EDGE,{"derivedFrom":subQ3}),1.0]])]});}
            var Q8;
            Q8=makeQuery(id+"F29.imprint","IMPRINT",FACE,{"disambiguationData":[TD([[makeQuery(id+"F29.imprint","IMPRINT",EDGE,{"derivedFrom":sQuery(id+"F29.wireOp",EDGE,"E89")}),-1.0]])]});
            var Q9;
            {var subQ0=sQuery(id+"F29.wireOp",EDGE,"E147");Q9=makeQuery(id+"F29.imprint","IMPRINT",FACE,{"disambiguationData":[TD([[makeQuery(id+"F29.imprint","IMPRINT",EDGE,{"derivedFrom":subQ0}),-1.0]])]});}
            extrude(context, id + "F31", {"entities" : qUnion([Q0, Q1, Q2, Q3, Q4, Q5, Q6, Q7, Q8, Q9]), "operationType" : NewBodyOperationType.ADD, "oppositeDirection" : true, "depth" : 15.24 * mm, "offsetDistance" : 25.4 * mm});
        }
    });
